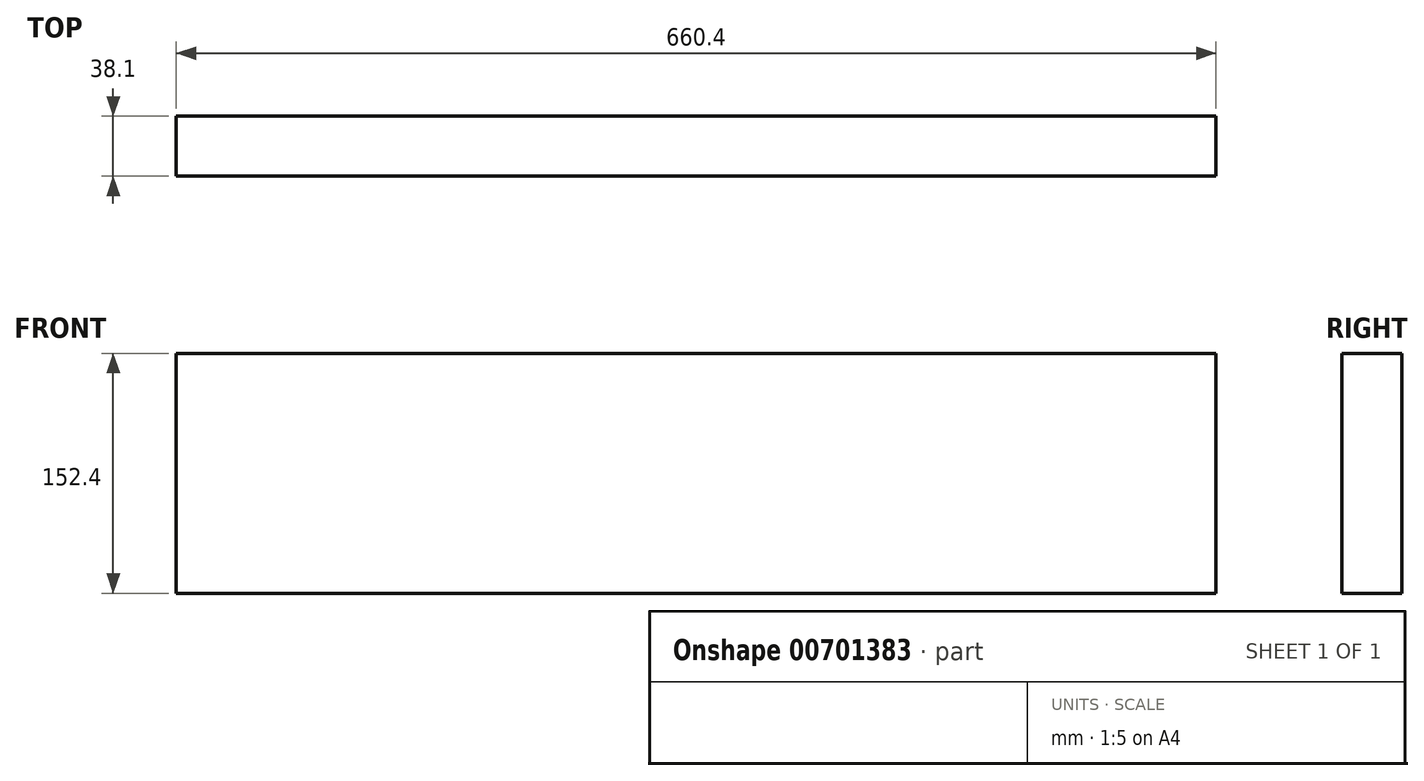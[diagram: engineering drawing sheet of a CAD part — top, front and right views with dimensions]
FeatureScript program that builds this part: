
annotation { "Feature Type Name" : "Feature", "Feature Type Description" : "" }
export const myFeature = defineFeature(function(context is Context, id is Id, definition is map)
    precondition{}
    {
        {
            var Q0;
            Q0=qCreatedBy(makeId("Front.planeOp"),FACE);
            var sketch = newSketch(context, id + "F0", { "sketchPlane" : qUnion([Q0])});
            skLineSegment(sketch, "E0.bottom", {"start": v(0, 0) * mm, "end": v(660.4, 0) * mm});
            skLineSegment(sketch, "E0.top", {"start": v(0, 152.4) * mm, "end": v(660.4, 152.4) * mm});
            skLineSegment(sketch, "E0.left", {"start": v(0, 0) * mm, "end": v(0, 152.4) * mm});
            skLineSegment(sketch, "E0.right", {"start": v(660.4, 0) * mm, "end": v(660.4, 152.4) * mm});
            skSolve(sketch);
        }
        {
            var Q0;
            Q0 = qSketchRegion(id + "F0", true);
            extrude(context, id + "F1", {"entities" : qUnion([Q0]), "depth" : 38.1 * mm, "offsetDistance" : 25.4 * mm});
        }
    });
